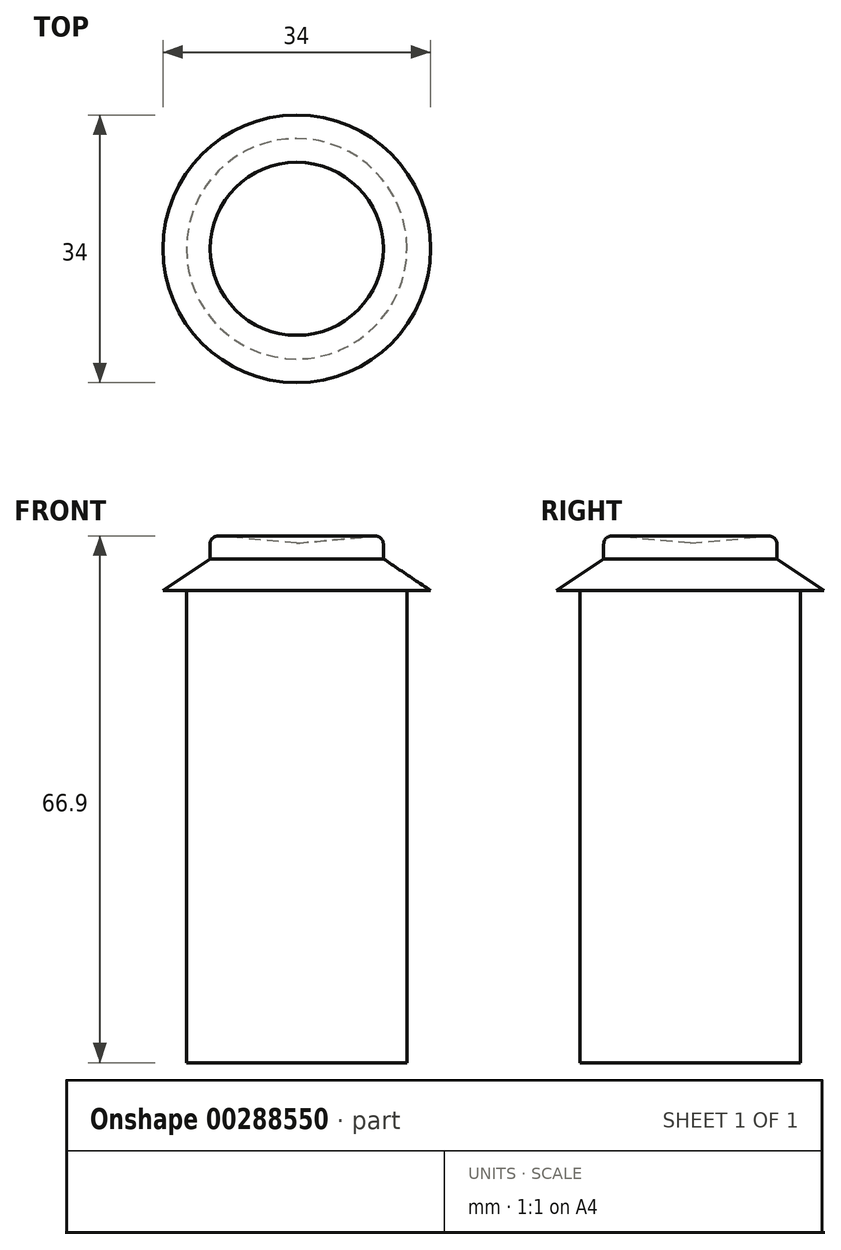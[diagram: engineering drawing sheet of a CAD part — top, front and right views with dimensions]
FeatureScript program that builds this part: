
annotation { "Feature Type Name" : "Feature", "Feature Type Description" : "" }
export const myFeature = defineFeature(function(context is Context, id is Id, definition is map)
    precondition{}
    {
        {
            var Q0;
            Q0=qCreatedBy(makeId("Front.planeOp"),FACE);
            var sketch = newSketch(context, id + "F0", { "sketchPlane" : qUnion([Q0])});
            skLineSegment(sketch, "E0", {"start": v(0, 0) * mm, "end": v(-14, 0) * mm});
            skLineSegment(sketch, "E1", {"start": v(-14, 0) * mm, "end": v(-14, 60) * mm});
            skLineSegment(sketch, "E2", {"start": v(-14, 60) * mm, "end": v(-17, 60) * mm});
            skLineSegment(sketch, "E3", {"start": v(0, 67) * mm, "end": v(-11, 67) * mm, "construction": true});
            skLineSegment(sketch, "E4", {"start": v(-11, 64) * mm, "end": v(-11, 67) * mm});
            skLineSegment(sketch, "E5", {"start": v(-17, 60) * mm, "end": v(-11, 64) * mm});
            skLineSegment(sketch, "E6", {"start": v(-11, 67) * mm, "end": v(0, 66) * mm});
            skLineSegment(sketch, "E7", {"start": v(0, 66) * mm, "end": v(0, 0) * mm});
            skLineSegment(sketch, "E8", {"start": v(0, 66) * mm, "end": v(0, 0) * mm, "construction": true});
            skSolve(sketch);
        }
        {
            var Q0;
            Q0=makeQuery(id+"F0.imprint","IMPRINT",FACE,{"disambiguationData":[TD([[makeQuery(id+"F0.imprint","IMPRINT",EDGE,{"derivedFrom":sQuery(id+"F0.wireOp",EDGE,"E0")}),-1.0]])]});
            var Q1;
            Q1=sQuery(id+"F0.wireOp",EDGE,"E7");
            revolve(context, id + "F1", {"entities" : qUnion([Q0]), "axis" : qUnion([Q1]), "revolveType" : RevolveType.FULL});
        }
        {
            var Q0;
            Q0=makeQuery(id+"F1.opRevolve","SWEPT_EDGE",EDGE,{"disambiguationData":[OSD([sQuery(id+"F0.wireOp",EDGE,"E4"),sQuery(id+"F0.wireOp",EDGE,"E6")])]});
            fillet(context, id + "F2", {"entities" : qUnion([Q0]), "radius" : 1 * mm, "tangentPropagation" : true, "allowEdgeOverflow" : false});
        }
    });
